# Revit family: Pebble_CB-275_BIM
name_source: partatom
category: Arredi
units: mm (PartAtom-declared; Revit-internal decimal feet)

## family parameters
Attiva taglio nelle viste = No
Basato su piano di lavoro = No
Condiviso = No
Numero OmniClass = 23.40.20.00
Origine composizione di rendering = Geometria famiglia
Punto di calcolo locali = No
Sempre verticale = Sì
Taglio con vuoti quando caricato = No
Titolo OmniClass = General Furniture and Specialties

## types (1)
- CB-275
    AVAILABLE FINISHES = Smoke powder coat finish (SP), or satin nickel (SN), satin brass (SB), bronze (BZ) or gunmetal (GM) nanoceramic coating.
    BASE MATERIAL = BASSAM_FELLOWS_ELEGANT_LEATHER_48027_OLIVE
    BIM BADGE = https://bim.archiproducts.com
    COLLECTION = Pebble
    DEPTH = 452 mm  [stored 1.48294 ft]
    Descrizione = Upholstered stool with steel base
    HEIGHT = 958 mm  [stored 3.14304 ft]
    MATERIAL DESCRIPTION = Foam upholstery, CARB2 plywood inner shell, tubular steel base.
    Modello = Pebble Padded Bar Stool
    PRODUCT CODE = CB-275
    PRODUCT SHEET = https://bim.archiproducts.com
    Produttore = BassamFellows
    Prospetto di default = 0 mm  [stored 0 ft]
    STRUCTURE MATERIAL = BASSAM_FELLOWS_BRONZE_BZ
    TECHNICAL SHEET = https://bassamfellows.com
    UPHOLSTERY MATERIAL = <Per categoria>
    URL = https://bassamfellows.com
    WIDTH = 450 mm  [stored 1.47638 ft]

note: [stored X ft] marks values corroborated as IEEE doubles in the binary element streams (Revit-internal decimal feet)

## geometry (parser evidence)
native form markers: Sweep x3
no freeform markers — native parametric forms only
